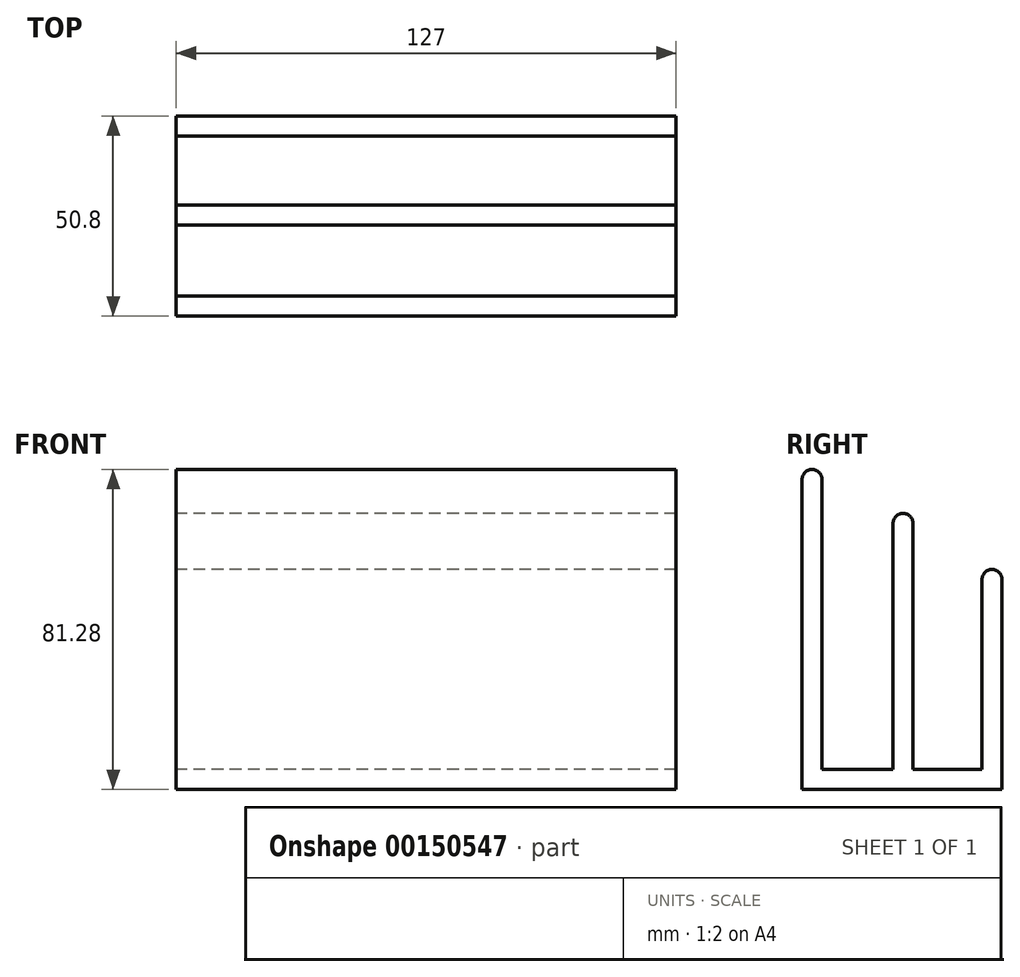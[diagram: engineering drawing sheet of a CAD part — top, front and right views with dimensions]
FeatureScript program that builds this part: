
annotation { "Feature Type Name" : "Feature", "Feature Type Description" : "" }
export const myFeature = defineFeature(function(context is Context, id is Id, definition is map)
    precondition{}
    {
        {
            var Q0;
            Q0=qCreatedBy(makeId("Right.planeOp"),FACE);
            var sketch = newSketch(context, id + "F0", { "sketchPlane" : qUnion([Q0])});
            skLineSegment(sketch, "E0.bottom", {"start": v(-25.4, 2.54) * mm, "end": v(25.4, 2.54) * mm});
            skLineSegment(sketch, "E0.top", {"start": v(-25.4, -2.54) * mm, "end": v(25.4, -2.54) * mm});
            skLineSegment(sketch, "E0.left", {"start": v(-25.4, 2.54) * mm, "end": v(-25.4, -2.54) * mm});
            skLineSegment(sketch, "E0.right", {"start": v(25.4, 2.54) * mm, "end": v(25.4, -2.54) * mm});
            skPoint(sketch, "E0.middle", {"position": v(0, 0) * mm});
            skLineSegment(sketch, "E1.bottom", {"start": v(-2.28, 2.54) * mm, "end": v(2.8, 2.54) * mm});
            skLineSegment(sketch, "E1.top", {"start": v(0.26, 67.6) * mm, "end": v(0.26, 67.6) * mm});
            skLineSegment(sketch, "E1.left", {"start": v(-2.28, 2.54) * mm, "end": v(-2.28, 65.05) * mm});
            skLineSegment(sketch, "E1.right", {"start": v(2.8, 2.54) * mm, "end": v(2.8, 65.05) * mm});
            skLineSegment(sketch, "E2.bottom", {"start": v(25.4, 2.54) * mm, "end": v(20.32, 2.54) * mm});
            skLineSegment(sketch, "E2.top", {"start": v(22.86, 53.34) * mm, "end": v(22.86, 53.34) * mm});
            skLineSegment(sketch, "E2.left", {"start": v(25.4, 2.54) * mm, "end": v(25.4, 50.8) * mm});
            skLineSegment(sketch, "E2.right", {"start": v(20.32, 2.54) * mm, "end": v(20.32, 50.8) * mm});
            skPoint(sketch, "E3.visualSharp", {"position": v(-2.28, 67.6) * mm});
            skArc(sketch, "E3.filletArc", {"start": v(0.26, 67.6) * mm, "mid": v(-1.54, 66.85) * mm, "end": v(-2.28, 65.05) * mm});
            skPoint(sketch, "E4.visualSharp", {"position": v(2.8, 67.6) * mm});
            skArc(sketch, "E4.filletArc", {"start": v(2.8, 65.05) * mm, "mid": v(2.05, 66.85) * mm, "end": v(0.26, 67.6) * mm});
            skPoint(sketch, "E5.visualSharp", {"position": v(20.32, 53.34) * mm});
            skArc(sketch, "E5.filletArc", {"start": v(22.86, 53.34) * mm, "mid": v(21.06, 52.6) * mm, "end": v(20.32, 50.8) * mm});
            skPoint(sketch, "E6.visualSharp", {"position": v(25.4, 53.34) * mm});
            skArc(sketch, "E6.filletArc", {"start": v(25.4, 50.8) * mm, "mid": v(24.66, 52.6) * mm, "end": v(22.86, 53.34) * mm});
            skLineSegment(sketch, "E7.bottom", {"start": v(-25.4, 2.54) * mm, "end": v(-20.32, 2.54) * mm});
            skLineSegment(sketch, "E7.top", {"start": v(-22.86, 78.74) * mm, "end": v(-22.86, 78.74) * mm});
            skLineSegment(sketch, "E7.left", {"start": v(-25.4, 2.54) * mm, "end": v(-25.4, 76.2) * mm});
            skLineSegment(sketch, "E7.right", {"start": v(-20.32, 2.54) * mm, "end": v(-20.32, 76.2) * mm});
            skPoint(sketch, "E8.visualSharp", {"position": v(-25.4, 78.74) * mm});
            skArc(sketch, "E8.filletArc", {"start": v(-22.86, 78.74) * mm, "mid": v(-24.66, 78) * mm, "end": v(-25.4, 76.2) * mm});
            skPoint(sketch, "E9.visualSharp", {"position": v(-20.32, 78.74) * mm});
            skArc(sketch, "E9.filletArc", {"start": v(-20.32, 76.2) * mm, "mid": v(-21.06, 78) * mm, "end": v(-22.86, 78.74) * mm});
            skSolve(sketch);
        }
        {
            var Q0;
            Q0=qSketchRegion(id+"F0",true);
            extrude(context, id + "F1", {"entities" : qUnion([Q0]), "depth" : 127 * mm});
        }
    });
